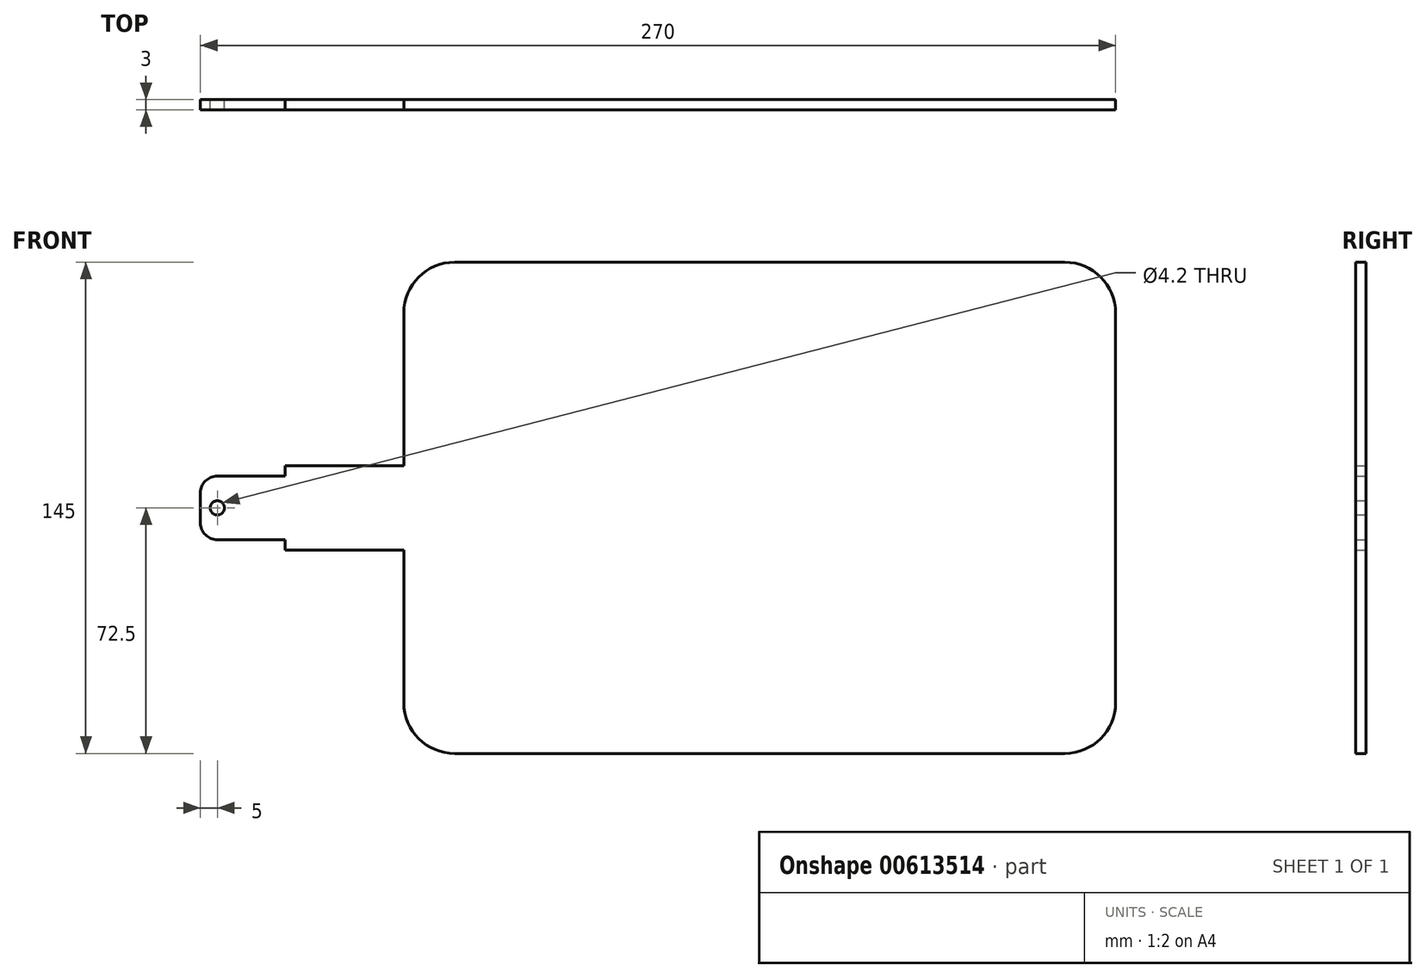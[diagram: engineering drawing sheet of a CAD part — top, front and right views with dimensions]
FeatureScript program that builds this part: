
annotation { "Feature Type Name" : "Feature", "Feature Type Description" : "" }
export const myFeature = defineFeature(function(context is Context, id is Id, definition is map)
    precondition{}
    {
        {
            var Q0;
            Q0=qCreatedBy(makeId("Front.planeOp"),FACE);
            var sketch = newSketch(context, id + "F0", { "sketchPlane" : qUnion([Q0])});
            skLineSegment(sketch, "E0.bottom", {"start": v(250, -72.5) * mm, "end": v(70, -72.5) * mm});
            skLineSegment(sketch, "E0.top", {"start": v(250, 72.5) * mm, "end": v(70, 72.5) * mm});
            skLineSegment(sketch, "E0.left", {"start": v(265, -57.5) * mm, "end": v(265, 57.5) * mm});
            skLineSegment(sketch, "E0.right", {"start": v(55, -57.5) * mm, "end": v(55, -12.4) * mm});
            skPoint(sketch, "E0.middle", {"position": v(160, 0) * mm});
            skPoint(sketch, "E1.visualSharp", {"position": v(55, 72.5) * mm});
            skArc(sketch, "E1.filletArc", {"start": v(70, 72.5) * mm, "mid": v(59.4, 68.1) * mm, "end": v(55, 57.5) * mm});
            skPoint(sketch, "E2.visualSharp", {"position": v(265, 72.5) * mm});
            skArc(sketch, "E2.filletArc", {"start": v(265, 57.5) * mm, "mid": v(260.6, 68.1) * mm, "end": v(250, 72.5) * mm});
            skPoint(sketch, "E3.visualSharp", {"position": v(265, -72.5) * mm});
            skArc(sketch, "E3.filletArc", {"start": v(250, -72.5) * mm, "mid": v(260.6, -68.1) * mm, "end": v(265, -57.5) * mm});
            skPoint(sketch, "E4.visualSharp", {"position": v(55, -72.5) * mm});
            skArc(sketch, "E4.filletArc", {"start": v(55, -57.5) * mm, "mid": v(59.4, -68.1) * mm, "end": v(70, -72.5) * mm});
            skLineSegment(sketch, "E5", {"start": v(-5, 0) * mm, "end": v(-5, -4.4) * mm});
            skLineSegment(sketch, "E6", {"start": v(0, -9.4) * mm, "end": v(20, -9.4) * mm});
            skLineSegment(sketch, "E7", {"start": v(20, -9.4) * mm, "end": v(20, -12.4) * mm});
            skLineSegment(sketch, "E8", {"start": v(20, -12.4) * mm, "end": v(55, -12.4) * mm});
            skLineSegment(sketch, "E9.MirrorCS", {"start": v(20, 9.4) * mm, "end": v(20, 12.4) * mm});
            skLineSegment(sketch, "E10.MirrorCS", {"start": v(0, 9.4) * mm, "end": v(20, 9.4) * mm});
            skLineSegment(sketch, "E11.MirrorCS", {"start": v(-5, 0) * mm, "end": v(-5, 4.4) * mm});
            skLineSegment(sketch, "E12.trimOffspring", {"start": v(55, 15.4) * mm, "end": v(55, 57.5) * mm});
            skCircle(sketch, "E13", {"center": v(0, 0) * mm, "radius": 2.1 * mm});
            skPoint(sketch, "E14.visualSharp", {"position": v(-5, 9.4) * mm});
            skArc(sketch, "E14.filletArc", {"start": v(0, 9.4) * mm, "mid": v(-3.54, 7.94) * mm, "end": v(-5, 4.4) * mm});
            skPoint(sketch, "E15.visualSharp", {"position": v(-5, -9.4) * mm});
            skArc(sketch, "E15.filletArc", {"start": v(-5, -4.4) * mm, "mid": v(-3.54, -7.94) * mm, "end": v(0, -9.4) * mm});
            skLineSegment(sketch, "E16.MirrorCS", {"start": v(20, 12.4) * mm, "end": v(55, 12.4) * mm});
            skLineSegment(sketch, "E17", {"start": v(55, 15.4) * mm, "end": v(55, 12.4) * mm});
            skPoint(sketch, "E18.orphan", {"position": v(20, 15.4) * mm});
            skSolve(sketch);
        }
        {
            var Q0;
            Q0=makeQuery(id+"F0.imprint","IMPRINT",FACE,{"disambiguationData":[TD([[makeQuery(id+"F0.imprint","IMPRINT",EDGE,{"derivedFrom":sQuery(id+"F0.wireOp",EDGE,"E0.bottom")}),-1.0]])]});
            extrude(context, id + "F1", {"entities" : qUnion([Q0]), "depth" : 3 * mm, "offsetDistance" : 25 * mm});
        }
    });
